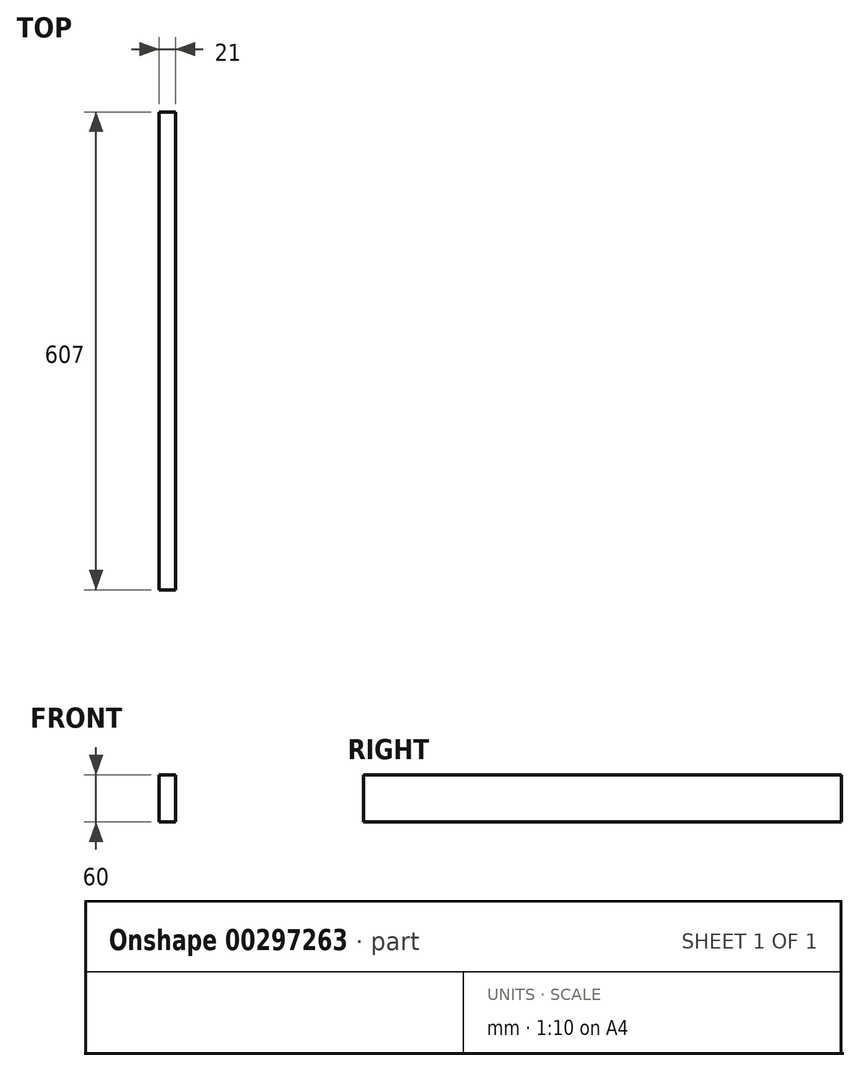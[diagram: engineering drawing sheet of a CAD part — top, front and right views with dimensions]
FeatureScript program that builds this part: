
annotation { "Feature Type Name" : "Feature", "Feature Type Description" : "" }
export const myFeature = defineFeature(function(context is Context, id is Id, definition is map)
    precondition{}
    {
        {
            var Q0;
            Q0=qCreatedBy(makeId("Right.planeOp"),FACE);
            var sketch = newSketch(context, id + "F0", { "sketchPlane" : qUnion([Q0])});
            skLineSegment(sketch, "E0.bottom", {"start": v(303.5, 30) * mm, "end": v(-303.5, 30) * mm});
            skLineSegment(sketch, "E0.top", {"start": v(303.5, -30) * mm, "end": v(-303.5, -30) * mm});
            skLineSegment(sketch, "E0.left", {"start": v(303.5, 30) * mm, "end": v(303.5, -30) * mm});
            skLineSegment(sketch, "E0.right", {"start": v(-303.5, 30) * mm, "end": v(-303.5, -30) * mm});
            skPoint(sketch, "E0.middle", {"position": v(0, 0) * mm});
            skSolve(sketch);
        }
        {
            var Q0;
            Q0 = qSketchRegion(id + "F0", true);
            extrude(context, id + "F1", {"entities" : qUnion([Q0]), "depth" : 21 * mm});
        }
    });
